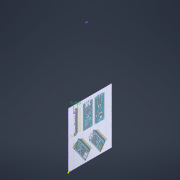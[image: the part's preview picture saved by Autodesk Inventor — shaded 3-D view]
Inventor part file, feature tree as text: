
AUTODESK INVENTOR PART (.ipt)
format: ipt  version: 2022 (Build 260153000, 153)  size: 310,784 bytes
history: native  units: mm
features: sketch x1, other x1
ambient origin geometry x8: Origin, YZ Plane, XZ Plane, XY Plane, X Axis, Y Axis, Z Axis, Center Point
feature tree (2):
  sketch  "Sketch1"  dims[d2=8.453482mm]
  other  "Image1"
